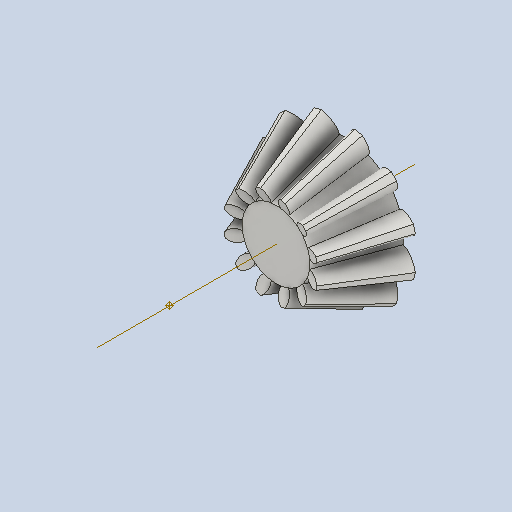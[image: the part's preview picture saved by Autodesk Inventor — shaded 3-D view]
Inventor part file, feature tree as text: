
AUTODESK INVENTOR PART (.ipt)
format: ipt  version: 2022 (Build 260153000, 153)  size: 464,896 bytes
history: native  units: in
note: dims shown in document units (in); Inventor stores cm internally (conversion verified against a paired STEP export)
features: other x30, sketch x1
ambient origin geometry x8: Origin, YZ Plane, XZ Plane, XY Plane, X Axis, Y Axis, Z Axis, Center Point
bodies: Solid1 (feature_tree)
feature tree (31):
  other  "Bevel Gear11_MIR2.ipt"
  other  "Solid1::Bevel Gear11_MIR2.ipt"
  other  "TaggingFeature1"
  other  "Teeth Body Sketch"
  other  "Start Sketch"
  other  "End Sketch"
  other  "End Sketch Right"
  other  "End Sketch Left"
  other  "Body Sketch"
  sketch  "Sketch6"  dims[d0=0.3937in d48=0.0in d49=0.0in d50=90.0deg d52=0.0in d53=0.0in d54=0.0in]
  other  "3D Sketch Right"
  other  "3D Sketch Left"
  other  "Mesh Plane"
  other  "Top Plane"
  other  "Mesh Plane2"
  other  "Tooth Plane"
  other  "End Plane"
  other  "End Plane Right"
  other  "End Plane Left"
  other  "Z Axis_1"
  other  "Top Point"
  other  "Start Point"
  other  "End Point"
  other  "Srf1"
  other  "Srf1::Derived"
  other  "Start plane iMate"
  other  "Mesh iMate2"
  other  "Axis Angle iMate"
  other  "Axis iMate"
  other  "Mesh iMate"
  other  "Intersection iMate"
